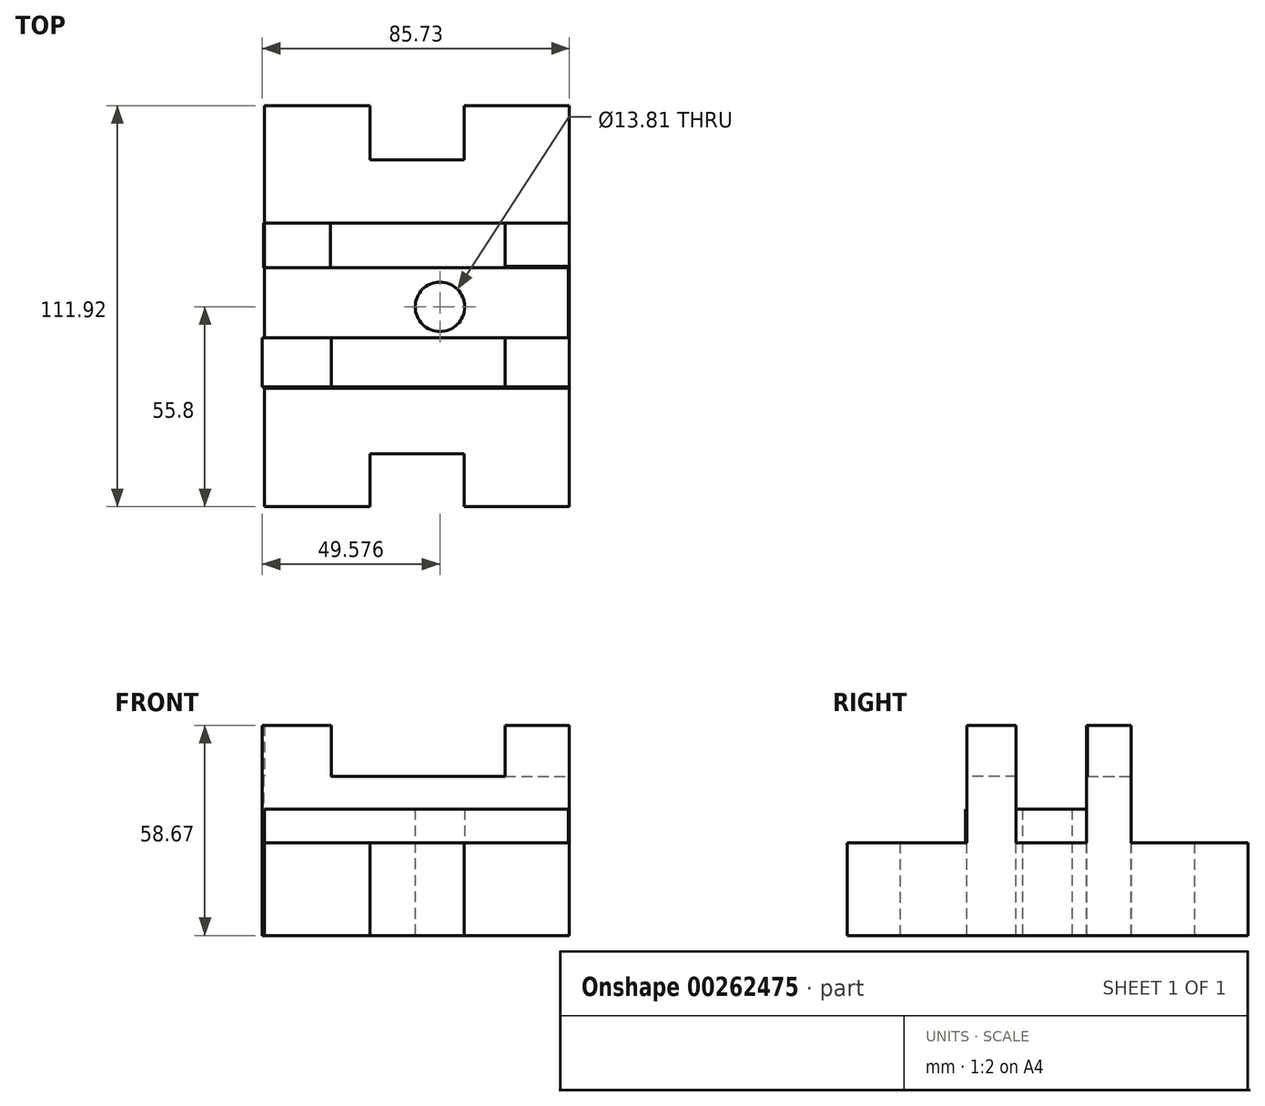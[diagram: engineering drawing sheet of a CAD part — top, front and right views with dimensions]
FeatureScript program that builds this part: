
annotation { "Feature Type Name" : "Feature", "Feature Type Description" : "" }
export const myFeature = defineFeature(function(context is Context, id is Id, definition is map)
    precondition{}
    {
        {
            var Q0;
            Q0=qCreatedBy(makeId("Top.planeOp"),FACE);
            var sketch = newSketch(context, id + "F0", { "sketchPlane" : qUnion([Q0])});
            skLineSegment(sketch, "E0.bottom", {"start": v(-42.87, 56.12) * mm, "end": v(42.21, 56.12) * mm});
            skLineSegment(sketch, "E0.top", {"start": v(-42.87, -55.8) * mm, "end": v(42.21, -55.8) * mm});
            skLineSegment(sketch, "E0.left", {"start": v(-42.87, 56.12) * mm, "end": v(-42.87, -55.8) * mm});
            skLineSegment(sketch, "E0.right", {"start": v(42.21, 56.12) * mm, "end": v(42.21, -55.8) * mm});
            skLineSegment(sketch, "E1.bottom", {"start": v(-13.42, -55.8) * mm, "end": v(12.76, -55.8) * mm});
            skLineSegment(sketch, "E1.top", {"start": v(-13.42, -41.07) * mm, "end": v(12.76, -41.07) * mm});
            skLineSegment(sketch, "E1.left", {"start": v(-13.42, -55.8) * mm, "end": v(-13.42, -41.07) * mm});
            skLineSegment(sketch, "E1.right", {"start": v(12.76, -55.8) * mm, "end": v(12.76, -41.07) * mm});
            skLineSegment(sketch, "E2", {"start": v(-13.42, 41.07) * mm, "end": v(12.76, 41.07) * mm});
            skLineSegment(sketch, "E3", {"start": v(12.76, 41.07) * mm, "end": v(12.76, 56.12) * mm});
            skLineSegment(sketch, "E4", {"start": v(12.76, 56.12) * mm, "end": v(-13.42, 56.12) * mm});
            skLineSegment(sketch, "E5", {"start": v(-13.42, 56.12) * mm, "end": v(-13.42, 41.07) * mm});
            skSolve(sketch);
        }
        {
            var Q0;
            {var subQ0=sQuery(id+"F0.wireOp",EDGE,"E0.left");Q0=makeQuery(id+"F0.imprint","IMPRINT",FACE,{"disambiguationData":[TD([[makeQuery(id+"F0.imprint","IMPRINT",EDGE,{"derivedFrom":subQ0}),1.0]])]});}
            extrude(context, id + "F1", {"entities" : qUnion([Q0]), "depth" : 25.9 * mm});
        }
        {
            var Q0;
            Q0=qCreatedBy(makeId("Top.planeOp"),FACE);
            var sketch = newSketch(context, id + "F2", { "sketchPlane" : qUnion([Q0])});
            skLineSegment(sketch, "E6.bottom", {"start": v(-42.87, 23.4) * mm, "end": v(41.89, 23.4) * mm});
            skLineSegment(sketch, "E6.top", {"start": v(-42.87, -22.74) * mm, "end": v(41.89, -22.74) * mm});
            skLineSegment(sketch, "E6.left", {"start": v(-42.87, 23.4) * mm, "end": v(-42.87, -22.74) * mm});
            skLineSegment(sketch, "E6.right", {"start": v(41.89, 23.4) * mm, "end": v(41.89, -22.74) * mm});
            skSolve(sketch);
        }
        {
            var Q0;
            Q0 = qSketchRegion(id + "F2", true);
            extrude(context, id + "F3", {"entities" : qUnion([Q0]), "operationType" : NewBodyOperationType.ADD, "depth" : 35.3 * mm});
        }
        {
            var Q0;
            Q0=qCreatedBy(makeId("Top.planeOp"),FACE);
            var sketch = newSketch(context, id + "F4", { "sketchPlane" : qUnion([Q0])});
            skLineSegment(sketch, "E7.bottom", {"start": v(-43.2, 23.4) * mm, "end": v(42.21, 23.4) * mm});
            skLineSegment(sketch, "E7.top", {"start": v(-43.2, 10.96) * mm, "end": v(42.21, 10.96) * mm});
            skLineSegment(sketch, "E7.left", {"start": v(-43.2, 23.4) * mm, "end": v(-43.2, 10.96) * mm});
            skLineSegment(sketch, "E7.right", {"start": v(42.21, 23.4) * mm, "end": v(42.21, 10.96) * mm});
            skLineSegment(sketch, "E8.bottom", {"start": v(-43.2, -22.42) * mm, "end": v(42.21, -22.42) * mm});
            skLineSegment(sketch, "E8.top", {"start": v(-43.2, -8.67) * mm, "end": v(42.21, -8.67) * mm});
            skLineSegment(sketch, "E8.left", {"start": v(-43.2, -22.42) * mm, "end": v(-43.2, -8.67) * mm});
            skLineSegment(sketch, "E8.right", {"start": v(42.21, -22.42) * mm, "end": v(42.21, -8.67) * mm});
            skSolve(sketch);
        }
        {
            var Q0;
            Q0 = qSketchRegion(id + "F4", true);
            extrude(context, id + "F5", {"entities" : qUnion([Q0]), "operationType" : NewBodyOperationType.ADD, "depth" : 44.45 * mm});
        }
        {
            var Q0;
            Q0=qCreatedBy(makeId("Top.planeOp"),FACE);
            var sketch = newSketch(context, id + "F6", { "sketchPlane" : qUnion([Q0])});
            skLineSegment(sketch, "E9.bottom", {"start": v(-42.87, 23.4) * mm, "end": v(-24.54, 23.4) * mm});
            skLineSegment(sketch, "E9.top", {"start": v(-42.87, 10.96) * mm, "end": v(-24.54, 10.96) * mm});
            skLineSegment(sketch, "E9.left", {"start": v(-42.87, 23.4) * mm, "end": v(-42.87, 10.96) * mm});
            skLineSegment(sketch, "E9.right", {"start": v(-24.54, 23.4) * mm, "end": v(-24.54, 10.96) * mm});
            skLineSegment(sketch, "E10.bottom", {"start": v(42.21, 23.4) * mm, "end": v(24.22, 23.4) * mm});
            skLineSegment(sketch, "E10.top", {"start": v(42.21, 11.29) * mm, "end": v(24.22, 11.29) * mm});
            skLineSegment(sketch, "E10.left", {"start": v(42.21, 23.4) * mm, "end": v(42.21, 11.29) * mm});
            skLineSegment(sketch, "E10.right", {"start": v(24.22, 23.4) * mm, "end": v(24.22, 11.29) * mm});
            skLineSegment(sketch, "E11.bottom", {"start": v(-43.52, -8.67) * mm, "end": v(-24.22, -8.67) * mm});
            skLineSegment(sketch, "E11.top", {"start": v(-43.52, -22.42) * mm, "end": v(-24.22, -22.42) * mm});
            skLineSegment(sketch, "E11.left", {"start": v(-43.52, -8.67) * mm, "end": v(-43.52, -22.42) * mm});
            skLineSegment(sketch, "E11.right", {"start": v(-24.22, -8.67) * mm, "end": v(-24.22, -22.42) * mm});
            skLineSegment(sketch, "E12.bottom", {"start": v(24.22, -22.42) * mm, "end": v(42.21, -22.42) * mm});
            skLineSegment(sketch, "E12.top", {"start": v(24.22, -8.67) * mm, "end": v(42.21, -8.67) * mm});
            skLineSegment(sketch, "E12.left", {"start": v(24.22, -22.42) * mm, "end": v(24.22, -8.67) * mm});
            skLineSegment(sketch, "E12.right", {"start": v(42.21, -22.42) * mm, "end": v(42.21, -8.67) * mm});
            skSolve(sketch);
        }
        {
            var Q0;
            Q0 = qSketchRegion(id + "F6", true);
            extrude(context, id + "F7", {"entities" : qUnion([Q0]), "operationType" : NewBodyOperationType.ADD, "depth" : 58.67 * mm});
        }
        {
            var Q0;
            Q0=qCreatedBy(makeId("Top.planeOp"),FACE);
            var sketch = newSketch(context, id + "F8", { "sketchPlane" : qUnion([Q0])});
            skCircle(sketch, "E13", {"center": v(6.06, 0) * mm, "radius": 6.9 * mm});
            skSolve(sketch);
        }
        {
            var Q0;
            Q0 = qSketchRegion(id + "F8", true);
            extrude(context, id + "F9", {"entities" : qUnion([Q0]), "operationType" : NewBodyOperationType.REMOVE, "depth" : 43.94 * mm});
        }
    });
